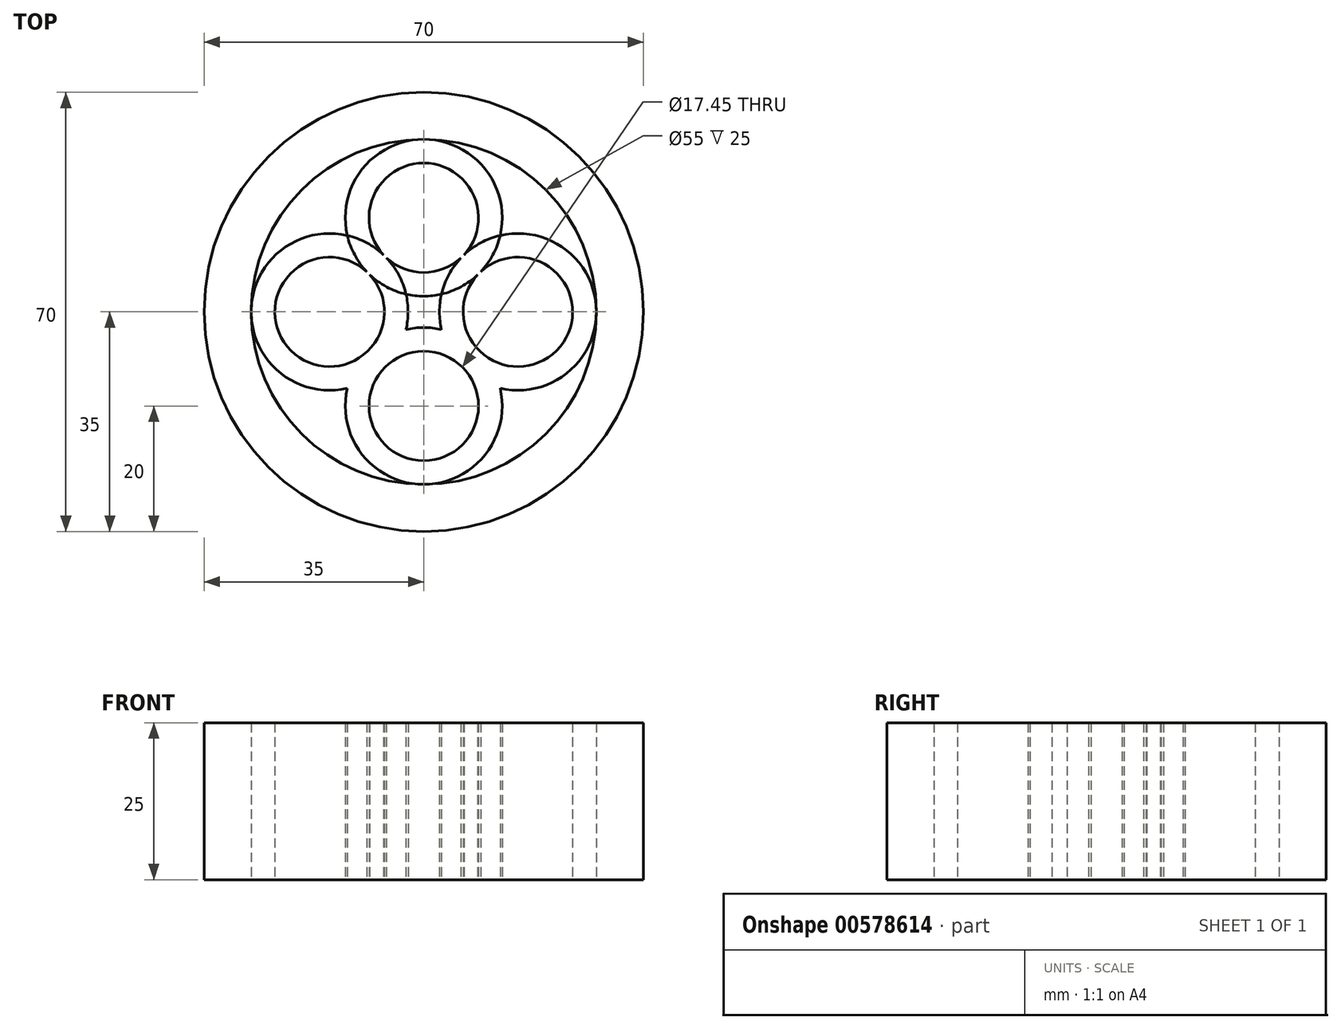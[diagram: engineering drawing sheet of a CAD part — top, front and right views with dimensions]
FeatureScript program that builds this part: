
annotation { "Feature Type Name" : "Feature", "Feature Type Description" : "" }
export const myFeature = defineFeature(function(context is Context, id is Id, definition is map)
    precondition{}
    {
        {
            var Q0;
            Q0=qCreatedBy(makeId("Top.planeOp"),FACE);
            var sketch = newSketch(context, id + "F0", { "sketchPlane" : qUnion([Q0])});
            skCircle(sketch, "E0", {"center": v(0, 0) * mm, "radius": 35 * mm});
            skCircle(sketch, "E1", {"center": v(0, 0) * mm, "radius": 27.5 * mm});
            skPoint(sketch, "E2", {"position": v(15, 0) * mm});
            skPoint(sketch, "E3", {"position": v(0, 15) * mm});
            skPoint(sketch, "E4", {"position": v(-15, 0) * mm});
            skPoint(sketch, "E5", {"position": v(0, -15) * mm});
            skCircle(sketch, "E6", {"center": v(0, 0) * mm, "radius": 1.75 * mm});
            skCircle(sketch, "E7", {"center": v(0, 0) * mm, "radius": 2.5 * mm});
            skCircle(sketch, "E8", {"center": v(15, 0) * mm, "radius": 12.5 * mm});
            skCircle(sketch, "E9", {"center": v(0, 15) * mm, "radius": 12.5 * mm});
            skCircle(sketch, "E10", {"center": v(0, -15) * mm, "radius": 12.5 * mm});
            skCircle(sketch, "E11", {"center": v(-15, 0) * mm, "radius": 12.5 * mm});
            skCircle(sketch, "E12", {"center": v(0, -15) * mm, "radius": 8.72 * mm});
            skCircle(sketch, "E13", {"center": v(15, 0) * mm, "radius": 8.72 * mm});
            skCircle(sketch, "E14", {"center": v(-15, 0) * mm, "radius": 8.72 * mm});
            skCircle(sketch, "E15", {"center": v(0, 15) * mm, "radius": 8.72 * mm});
            skSolve(sketch);
        }
        {
            var Q0;
            Q0=makeQuery(id+"F0.imprint","IMPRINT",FACE,{"disambiguationData":[TD([[makeQuery(id+"F0.imprint","IMPRINT",EDGE,{"derivedFrom":sQuery(id+"F0.wireOp",EDGE,"E0")}),1.0]])]});
            var Q1;
            {var subQ0=sQuery(id+"F0.wireOp",EDGE,"E11");var subQ4=sQuery(id+"F0.wireOp",EDGE,"E9");var subQ5=makeQuery(id+"F0.imprint","INTERSECT",VERTEX,{"disambiguationData":[OD(0.0)],"derivedFrom":[subQ4,subQ0]});Q1=makeQuery(id+"F0.imprint","IMPRINT",FACE,{"disambiguationData":[TD([[makeQuery(id+"F0.imprint","IMPRINT",EDGE,{"disambiguationData":[TD([[subQ5,-1.0]])],"derivedFrom":subQ4}),-1.0]])]});}
            var Q2;
            {var subQ3=sQuery(id+"F0.wireOp",EDGE,"E12");var subQ6=sQuery(id+"F0.wireOp",EDGE,"E8");var subQ8=makeQuery(id+"F0.imprint","INTERSECT",VERTEX,{"disambiguationData":[OD(1.0)],"derivedFrom":[subQ6,subQ3]});Q2=makeQuery(id+"F0.imprint","IMPRINT",FACE,{"disambiguationData":[TD([[makeQuery(id+"F0.imprint","IMPRINT",EDGE,{"disambiguationData":[TD([[subQ8,-1.0]])],"derivedFrom":subQ6}),-1.0]])]});}
            var Q3;
            {var subQ0=sQuery(id+"F0.wireOp",EDGE,"E11");var subQ1=sQuery(id+"F0.wireOp",EDGE,"E10");var subQ2=makeQuery(id+"F0.imprint","INTERSECT",VERTEX,{"disambiguationData":[OD(0.0)],"derivedFrom":[subQ1,subQ0]});Q3=makeQuery(id+"F0.imprint","IMPRINT",FACE,{"disambiguationData":[TD([[makeQuery(id+"F0.imprint","IMPRINT",EDGE,{"disambiguationData":[TD([[subQ2,-1.0]])],"derivedFrom":subQ1}),1.0]])]});}
            var Q4;
            {var subQ4=sQuery(id+"F0.wireOp",EDGE,"E9");var subQ6=sQuery(id+"F0.wireOp",EDGE,"E14");var subQ8=makeQuery(id+"F0.imprint","INTERSECT",VERTEX,{"disambiguationData":[OD(1.0)],"derivedFrom":[subQ4,subQ6]});Q4=makeQuery(id+"F0.imprint","IMPRINT",FACE,{"disambiguationData":[TD([[makeQuery(id+"F0.imprint","IMPRINT",EDGE,{"disambiguationData":[TD([[subQ8,-1.0]])],"derivedFrom":subQ4}),-1.0]])]});}
            var Q5;
            {var subQ3=sQuery(id+"F0.wireOp",EDGE,"E15");var subQ5=sQuery(id+"F0.wireOp",EDGE,"E8");var subQ6=makeQuery(id+"F0.imprint","INTERSECT",VERTEX,{"disambiguationData":[OD(1.0)],"derivedFrom":[subQ5,subQ3]});Q5=makeQuery(id+"F0.imprint","IMPRINT",FACE,{"disambiguationData":[TD([[makeQuery(id+"F0.imprint","IMPRINT",EDGE,{"disambiguationData":[TD([[subQ6,-1.0]])],"derivedFrom":subQ5}),-1.0]])]});}
            var Q6;
            {var subQ0=sQuery(id+"F0.wireOp",EDGE,"E10");var subQ6=sQuery(id+"F0.wireOp",EDGE,"E8");var subQ7=makeQuery(id+"F0.imprint","INTERSECT",VERTEX,{"disambiguationData":[OD(0.0)],"derivedFrom":[subQ6,subQ0]});Q6=makeQuery(id+"F0.imprint","IMPRINT",FACE,{"disambiguationData":[TD([[makeQuery(id+"F0.imprint","IMPRINT",EDGE,{"disambiguationData":[TD([[subQ7,-1.0]])],"derivedFrom":subQ6}),-1.0]])]});}
            var Q7;
            {var subQ0=sQuery(id+"F0.wireOp",EDGE,"E10");var subQ1=sQuery(id+"F0.wireOp",EDGE,"E8");var subQ2=makeQuery(id+"F0.imprint","INTERSECT",VERTEX,{"disambiguationData":[OD(0.0)],"derivedFrom":[subQ1,subQ0]});Q7=makeQuery(id+"F0.imprint","IMPRINT",FACE,{"disambiguationData":[TD([[makeQuery(id+"F0.imprint","IMPRINT",EDGE,{"disambiguationData":[TD([[subQ2,-1.0]])],"derivedFrom":subQ1}),1.0]])]});}
            var Q8;
            {var subQ1=sQuery(id+"F0.wireOp",EDGE,"E8");var subQ8=makeQuery(id+"F0.imprint","INTERSECT",VERTEX,{"derivedFrom":[sQuery(id+"F0.wireOp",EDGE,"E7"),subQ1]});Q8=makeQuery(id+"F0.imprint","IMPRINT",FACE,{"disambiguationData":[TD([[makeQuery(id+"F0.imprint","IMPRINT",EDGE,{"disambiguationData":[TD([[subQ8,1.0]])],"derivedFrom":subQ1}),1.0]])]});}
            var Q9;
            {var subQ1=sQuery(id+"F0.wireOp",EDGE,"E8");var subQ5=makeQuery(id+"F0.imprint","INTERSECT",VERTEX,{"derivedFrom":[sQuery(id+"F0.wireOp",EDGE,"E1"),subQ1]});Q9=makeQuery(id+"F0.imprint","IMPRINT",FACE,{"disambiguationData":[TD([[makeQuery(id+"F0.imprint","IMPRINT",EDGE,{"disambiguationData":[TD([[subQ5,-1.0]])],"derivedFrom":subQ1}),1.0]])]});}
            var Q10;
            {var subQ1=sQuery(id+"F0.wireOp",EDGE,"E9");var subQ5=sQuery(id+"F0.wireOp",EDGE,"E8");var subQ8=makeQuery(id+"F0.imprint","INTERSECT",VERTEX,{"disambiguationData":[OD(0.0)],"derivedFrom":[subQ5,subQ1]});Q10=makeQuery(id+"F0.imprint","IMPRINT",FACE,{"disambiguationData":[TD([[makeQuery(id+"F0.imprint","IMPRINT",EDGE,{"disambiguationData":[TD([[subQ8,-1.0]])],"derivedFrom":subQ5}),-1.0]])]});}
            extrude(context, id + "F1", {"entities" : qUnion([Q0, Q1, Q2, Q3, Q4, Q5, Q6, Q7, Q8, Q9, Q10]), "depth" : 25 * mm, "offsetDistance" : 25 * mm});
        }
    });
